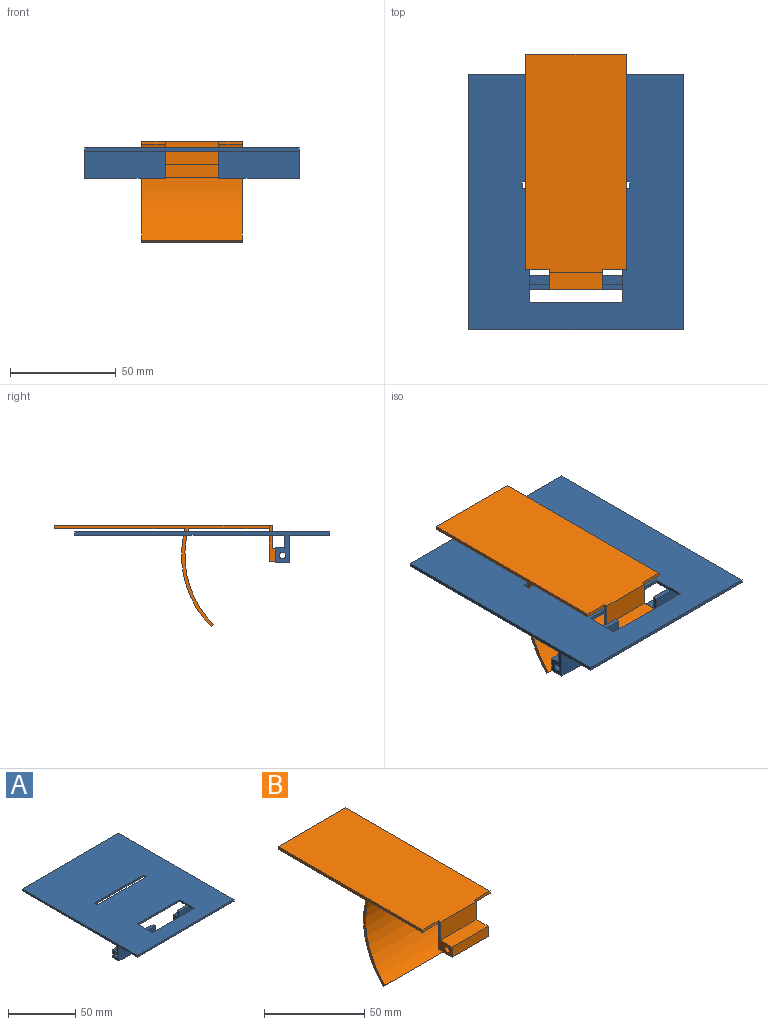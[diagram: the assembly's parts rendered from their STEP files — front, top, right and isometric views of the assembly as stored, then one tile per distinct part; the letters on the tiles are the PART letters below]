
ASSEMBLY  parts=2 mates=1
PART A: 31 faces, bbox 101.6x120.7x14.4 mm
  f0: plane 38.1x12.86mm, normal (0,-1,0), area 490mm2, adj f1,f3,f16,f21,f29
  f1: plane 38.1x6.74mm, normal (0,0,-1), area 256.8mm2, adj f0,f16,f25,f29
  f2: plane 38.1x6.85mm, normal (0,1,0), area 261mm2, adj f14,f24,f26,f30
  f3: plane 9.53x2.42mm, normal (0,0,1), area 23.1mm2, adj f0,f6,f19,f29
  f4: plane 38.1x4.32mm, normal (0,0,1), area 164.6mm2, adj f6,f16,f25,f29
  f5: cylinder r=1.59mm len=38.1mm, axis (1,0,0), area 380mm2, adj f16,f29
  f6: plane 38.1x6.01mm, normal (0,1,0), area 229mm2, adj f3,f4,f7,f16,f29
  f7: plane 101.6x99.25mm, normal (0,0,-1), area 9603.7mm2, adj f6,f9,f10,f11,f12,f13,f14,f16
  f8: plane 44.45x1.59mm, normal (0,1,0), area 70.6mm2, adj f9,f19,f20,f21
  f9: plane 15.88x1.59mm, normal (1,0,0), area 25.2mm2, adj f7,f8,f10,f20,f21,f22
  f10: plane 44.45x1.59mm, normal (0,-1,0), area 70.6mm2, adj f7,f9,f19,f20
  f11: plane 3.18x1.59mm, normal (1,0,0), area 5mm2, adj f7,f12,f17,f20
  f12: plane 50.8x1.59mm, normal (0,-1,0), area 80.6mm2, adj f7,f11,f13,f20
  f13: plane 3.18x1.59mm, normal (-1,0,0), area 5mm2, adj f7,f12,f17,f20
  f14: plane 120.65x14.45mm, normal (-1,0,0), area 244.4mm2, adj f2,f7,f15,f18,f20,f21,f23,f24
  f15: plane 101.6x1.59mm, normal (0,-1,0), area 161.3mm2, adj f14,f16,f20,f21
  f16: plane 120.65x14.45mm, normal (1,0,0), area 244.4mm2, adj f0,f1,f4,f5,f6,f7,f15,f18
  f17: plane 50.8x1.59mm, normal (0,1,0), area 80.6mm2, adj f7,f11,f13,f20
  f18: plane 101.6x1.59mm, normal (0,1,0), area 161.3mm2, adj f7,f14,f16,f20
  f19: plane 15.88x1.59mm, normal (-1,0,0), area 25.2mm2, adj f3,f7,f8,f10,f20,f21
  f20: plane 120.65x101.6mm, normal (0,0,1), area 11391.1mm2, adj f8,f9,f10,f11,f12,f13,f14,f15
  f21: plane 101.6x18.98mm, normal (0,0,-1), area 1649.1mm2, adj f0,f8,f9,f14,f15,f16,f19,f23
  f22: plane 9.53x2.42mm, normal (0,0,1), area 23.1mm2, adj f9,f23,f28,f30
  f23: plane 38.1x12.86mm, normal (0,-1,0), area 490mm2, adj f14,f21,f22,f24,f30
  f24: plane 38.1x6.74mm, normal (0,0,-1), area 256.8mm2, adj f2,f14,f23,f30
  f25: plane 38.1x6.85mm, normal (0,1,0), area 261mm2, adj f1,f4,f16,f29
  f26: plane 38.1x4.32mm, normal (0,0,1), area 164.6mm2, adj f2,f14,f28,f30
  f27: cylinder r=1.59mm len=38.1mm, axis (1,0,0), area 380mm2, adj f14,f30
  f28: plane 38.1x6.01mm, normal (0,1,0), area 229mm2, adj f7,f14,f22,f26,f30
  f29: plane 12.86x6.74mm, normal (-1,0,0), area 52.8mm2, adj f0,f1,f3,f4,f5,f6,f25
  f30: plane 12.86x6.74mm, normal (1,0,0), area 52.8mm2, adj f2,f22,f23,f24,f26,f27,f28
PART B: 19 faces, bbox 47.6x111.4x48.1 mm
  f0: plane 47.63x38.1mm, normal (0,0,-1), area 1814.5mm2, adj f3,f7,f8,f12,f14,f18
  f1: plane 25.4x6.19mm, normal (0,-1,0), area 157.2mm2, adj f2,f5,f11,f13
  f2: plane 25.4x9.81mm, normal (0,0,-1), area 249.1mm2, adj f1,f3,f11,f13
  f3: plane 25.4x15.61mm, normal (0,1,0), area 396.5mm2, adj f0,f2,f11,f13
  f4: plane 25.4x11.01mm, normal (0,-1,0), area 279.6mm2, adj f5,f6,f11,f13
  f5: plane 25.4x8.22mm, normal (0,0,1), area 208.8mm2, adj f1,f4,f11,f13
  f6: plane 103.19x47.63mm, normal (0,0,1), area 4879mm2, adj f4,f7,f8,f10,f11,f12,f13,f14
  f7: plane 101.6x48.1mm, normal (1,0,0), area 240.3mm2, adj f0,f6,f9,f10,f12,f16,f17,f18
  f8: plane 101.6x48.1mm, normal (-1,0,0), area 240.3mm2, adj f0,f6,f9,f10,f14,f16,f17,f18
  f9: plane 61.85x47.63mm, normal (0,0,-1), area 2945.7mm2, adj f7,f8,f10,f16
  f10: plane 47.63x1.59mm, normal (0,1,0), area 75.6mm2, adj f6,f7,f8,f9
  f11: plane 17.2x9.81mm, normal (1,0,0), area 70.3mm2, adj f1,f2,f3,f4,f5,f6,f12,f15
  f12: plane 11.11x1.59mm, normal (0,-1,0), area 17.6mm2, adj f0,f6,f7,f11
  f13: plane 17.2x9.81mm, normal (-1,0,0), area 70.3mm2, adj f1,f2,f3,f4,f5,f6,f14,f15
  f14: plane 11.11x1.59mm, normal (0,-1,0), area 17.6mm2, adj f0,f6,f8,f13
  f15: cylinder r=1.59mm len=25.4mm, axis (-1,0,0), area 253.4mm2, adj f11,f13
  f16: cylinder r=47.82mm len=47.63mm, axis (-1,0,0), area 2400.7mm2, adj f7,f8,f9,f17
  f17: plane 47.63x1.12mm, normal (0,-0.71,-0.71), area 75.6mm2, adj f7,f8,f16,f18
  f18: cylinder r=46.23mm len=47.63mm, axis (-1,0,0), area 2341.9mm2, adj f0,f7,f8,f17
PLACE A t=(71.91,-39.46,32.42)mm fixed
PLACE B rot(axis=(1,0,0),0deg) t=(98.9,-10.89,35.59)mm
MATE revolute B.f15 <-> A.f5  axis (-1,0,0) through (110.01,-17.24,22.89)mm
